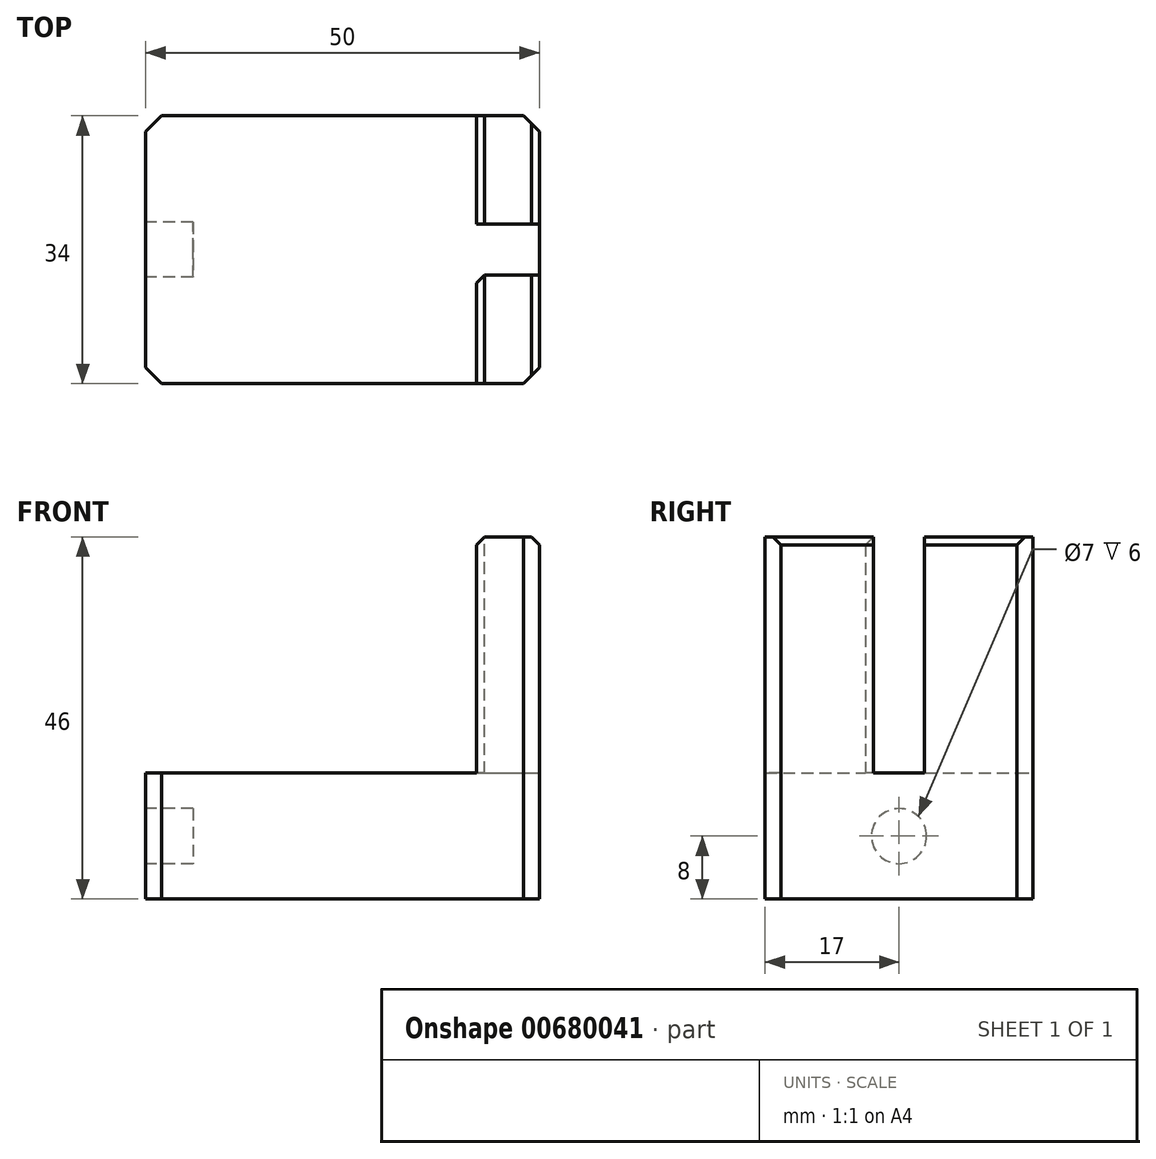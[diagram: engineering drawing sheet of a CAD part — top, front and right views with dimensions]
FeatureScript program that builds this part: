
annotation { "Feature Type Name" : "Feature", "Feature Type Description" : "" }
export const myFeature = defineFeature(function(context is Context, id is Id, definition is map)
    precondition{}
    {
        {
            var Q0;
            Q0=qCreatedBy(makeId("Front.planeOp"),FACE);
            var sketch = newSketch(context, id + "F0", { "sketchPlane" : qUnion([Q0])});
            skLineSegment(sketch, "E0.bottom", {"start": v(-25, 8) * mm, "end": v(-20, 8) * mm});
            skLineSegment(sketch, "E0.top", {"start": v(-25, -8) * mm, "end": v(25, -8) * mm});
            skLineSegment(sketch, "E0.left", {"start": v(-25, 8) * mm, "end": v(-25, -8) * mm});
            skLineSegment(sketch, "E0.right", {"start": v(25, 38) * mm, "end": v(25, -8) * mm});
            skPoint(sketch, "E0.middle", {"position": v(0, 0) * mm});
            skLineSegment(sketch, "E1.0", {"start": v(-20, 8) * mm, "end": v(-20, 8) * mm});
            skLineSegment(sketch, "E2.0", {"start": v(-20, 8) * mm, "end": v(17, 8) * mm});
            skLineSegment(sketch, "E3.0", {"start": v(17, 38) * mm, "end": v(17, 8) * mm});
            skPoint(sketch, "E4.orphan", {"position": v(25, 8) * mm});
            skLineSegment(sketch, "E5.trimOffspring", {"start": v(17, 38) * mm, "end": v(25, 38) * mm});
            skSolve(sketch);
        }
        {
            var Q0;
            Q0=qSketchRegion(id+"F0",true);
            extrude(context, id + "F1", {"entities" : qUnion([Q0]), "depth" : 34 * mm, "offsetDistance" : 25 * mm});
        }
        {
            var Q0;
            Q0=makeQuery(id+"F1.opExtrude","SWEPT_FACE",FACE,{"disambiguationData":[OSD([sQuery(id+"F0.wireOp",EDGE,"E0.right")])]});
            var sketch = newSketch(context, id + "F2", { "sketchPlane" : qUnion([Q0])});
            skLineSegment(sketch, "E6.bottom", {"start": v(-20.25, 38) * mm, "end": v(-13.75, 38) * mm});
            skLineSegment(sketch, "E6.top", {"start": v(-20.25, 8) * mm, "end": v(-13.75, 8) * mm});
            skLineSegment(sketch, "E6.left", {"start": v(-20.25, 38) * mm, "end": v(-20.25, 8) * mm});
            skLineSegment(sketch, "E6.right", {"start": v(-13.75, 38) * mm, "end": v(-13.75, 8) * mm});
            skSolve(sketch);
        }
        {
            var Q0;
            Q0=qSketchRegion(id+"F2",true);
            var Q1;
            Q1=makeQuery(id+"F1.opExtrude","SWEPT_FACE",FACE,{"disambiguationData":[OSD([sQuery(id+"F0.wireOp",EDGE,"E3.0")])]});
            extrude(context, id + "F3", {"entities" : qUnion([Q0]), "operationType" : NewBodyOperationType.REMOVE, "endBound" : BoundingType.UP_TO_SURFACE, "oppositeDirection" : true, "depth" : 25 * mm, "endBoundEntityFace" : qUnion([Q1]), "offsetDistance" : 25 * mm});
        }
        {
            var Q0;
            Q0=makeQuery(id+"F1.opExtrude","SWEPT_FACE",FACE,{"disambiguationData":[OSD([sQuery(id+"F0.wireOp",EDGE,"E0.left")])]});
            var sketch = newSketch(context, id + "F4", { "sketchPlane" : qUnion([Q0])});
            skCircle(sketch, "E7", {"center": v(17, 0) * mm, "radius": 3.5 * mm});
            skSolve(sketch);
        }
        {
            var Q0;
            Q0=qSketchRegion(id+"F4",true);
            extrude(context, id + "F5", {"entities" : qUnion([Q0]), "operationType" : NewBodyOperationType.REMOVE, "oppositeDirection" : true, "depth" : 6 * mm, "offsetDistance" : 25 * mm});
        }
        {
            var Q0;
            {var subQ0=sQuery(id+"F0.wireOp",EDGE,"E5.trimOffspring");var subQ1=sQuery(id+"F0.wireOp",EDGE,"E0.right");Q0=makeQuery(id+"F3.boolean.opBoolean","SPLIT",EDGE,{"disambiguationData":[TD([makeQuery(id+"F3.opExtrude","SWEPT_FACE",FACE,{"disambiguationData":[OSD([sQuery(id+"F2.wireOp",EDGE,"E6.left")])]})])],"derivedFrom":makeQuery(id+"F1.opExtrude","SWEPT_EDGE",EDGE,{"disambiguationData":[OSD([subQ1,subQ0])]})});}
            var Q1;
            {var subQ0=sQuery(id+"F0.wireOp",EDGE,"E5.trimOffspring");var subQ1=sQuery(id+"F0.wireOp",EDGE,"E0.right");Q1=makeQuery(id+"F3.boolean.opBoolean","SPLIT",EDGE,{"disambiguationData":[TD([makeQuery(id+"F3.opExtrude","SWEPT_FACE",FACE,{"disambiguationData":[OSD([sQuery(id+"F2.wireOp",EDGE,"E6.right")])]})])],"derivedFrom":makeQuery(id+"F1.opExtrude","SWEPT_EDGE",EDGE,{"disambiguationData":[OSD([subQ1,subQ0])]})});}
            var Q2;
            {var subQ0=sQuery(id+"F0.wireOp",EDGE,"E5.trimOffspring");var subQ1=sQuery(id+"F0.wireOp",EDGE,"E3.0");Q2=makeQuery(id+"F3.boolean.opBoolean","SPLIT",EDGE,{"disambiguationData":[TD([makeQuery(id+"F3.opExtrude","SWEPT_FACE",FACE,{"disambiguationData":[OSD([sQuery(id+"F2.wireOp",EDGE,"E6.right")])]})])],"derivedFrom":makeQuery(id+"F1.opExtrude","SWEPT_EDGE",EDGE,{"disambiguationData":[OSD([subQ1,subQ0])]})});}
            var Q3;
            {var subQ0=sQuery(id+"F0.wireOp",EDGE,"E5.trimOffspring");var subQ1=sQuery(id+"F0.wireOp",EDGE,"E3.0");Q3=makeQuery(id+"F3.boolean.opBoolean","SPLIT",EDGE,{"disambiguationData":[TD([makeQuery(id+"F3.opExtrude","SWEPT_FACE",FACE,{"disambiguationData":[OSD([sQuery(id+"F2.wireOp",EDGE,"E6.left")])]})])],"derivedFrom":makeQuery(id+"F1.opExtrude","SWEPT_EDGE",EDGE,{"disambiguationData":[OSD([subQ1,subQ0])]})});}
            var Q4;
            Q4=makeQuery(id+"F3.boolean.opBoolean","COPY",EDGE,{"derivedFrom":makeQuery(id+"F3.opExtrude","CAP_EDGE",EDGE,{"disambiguationData":[OSD([sQuery(id+"F2.wireOp",EDGE,"E6.right")])],"isStart":false})});
            var Q5;
            Q5=makeQuery(id+"F3.boolean.opBoolean","COPY",EDGE,{"derivedFrom":makeQuery(id+"F3.opExtrude","CAP_EDGE",EDGE,{"disambiguationData":[OSD([sQuery(id+"F2.wireOp",EDGE,"E6.left")])],"isStart":false})});
            chamfer(context, id + "F6", {"entities" : qUnion([Q0, Q1, Q2, Q3, Q4, Q5]), "width" : 1 * mm, "tangentPropagation" : true});
        }
        {
            var Q0;
            Q0=makeQuery(id+"F1.opExtrude","CAP_EDGE",EDGE,{"disambiguationData":[OSD([sQuery(id+"F0.wireOp",EDGE,"E0.right")])],"isStart":false});
            var Q1;
            Q1=makeQuery(id+"F1.opExtrude","CAP_EDGE",EDGE,{"disambiguationData":[OSD([sQuery(id+"F0.wireOp",EDGE,"E0.left")])],"isStart":false});
            var Q2;
            Q2=makeQuery(id+"F1.opExtrude","CAP_EDGE",EDGE,{"disambiguationData":[OSD([sQuery(id+"F0.wireOp",EDGE,"E0.right")])],"isStart":true});
            var Q3;
            Q3=makeQuery(id+"F1.opExtrude","CAP_EDGE",EDGE,{"disambiguationData":[OSD([sQuery(id+"F0.wireOp",EDGE,"E0.left")])],"isStart":true});
            chamfer(context, id + "F7", {"entities" : qUnion([Q0, Q1, Q2, Q3]), "width" : 2 * mm, "tangentPropagation" : true});
        }
    });
